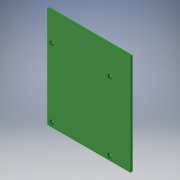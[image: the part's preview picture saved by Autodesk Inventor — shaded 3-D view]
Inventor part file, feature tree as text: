
AUTODESK INVENTOR PART (.ipt)
format: ipt  version: 2019.4 (Build 234330000, 330)  size: 112,640 bytes
history: native  units: mm
features: extrude x1, sketch x1, imported_body x1
ambient origin geometry x8: Origin, YZ Plane, XZ Plane, XY Plane, X Axis, Y Axis, Z Axis, Center Point
bodies: Solid1 (feature_tree)
feature tree (3):
  extrude  "Extrusion1"  Depth=10.0mm
  sketch  "Sketch1"  dims[d0=3.5mm d1=3.5mm d2=3.5mm d3=20.0mm d5=49.0mm d6=20.0mm d8=58.0mm d11=10.0mm d12=0.0mm]
  imported_body  "Base1"
